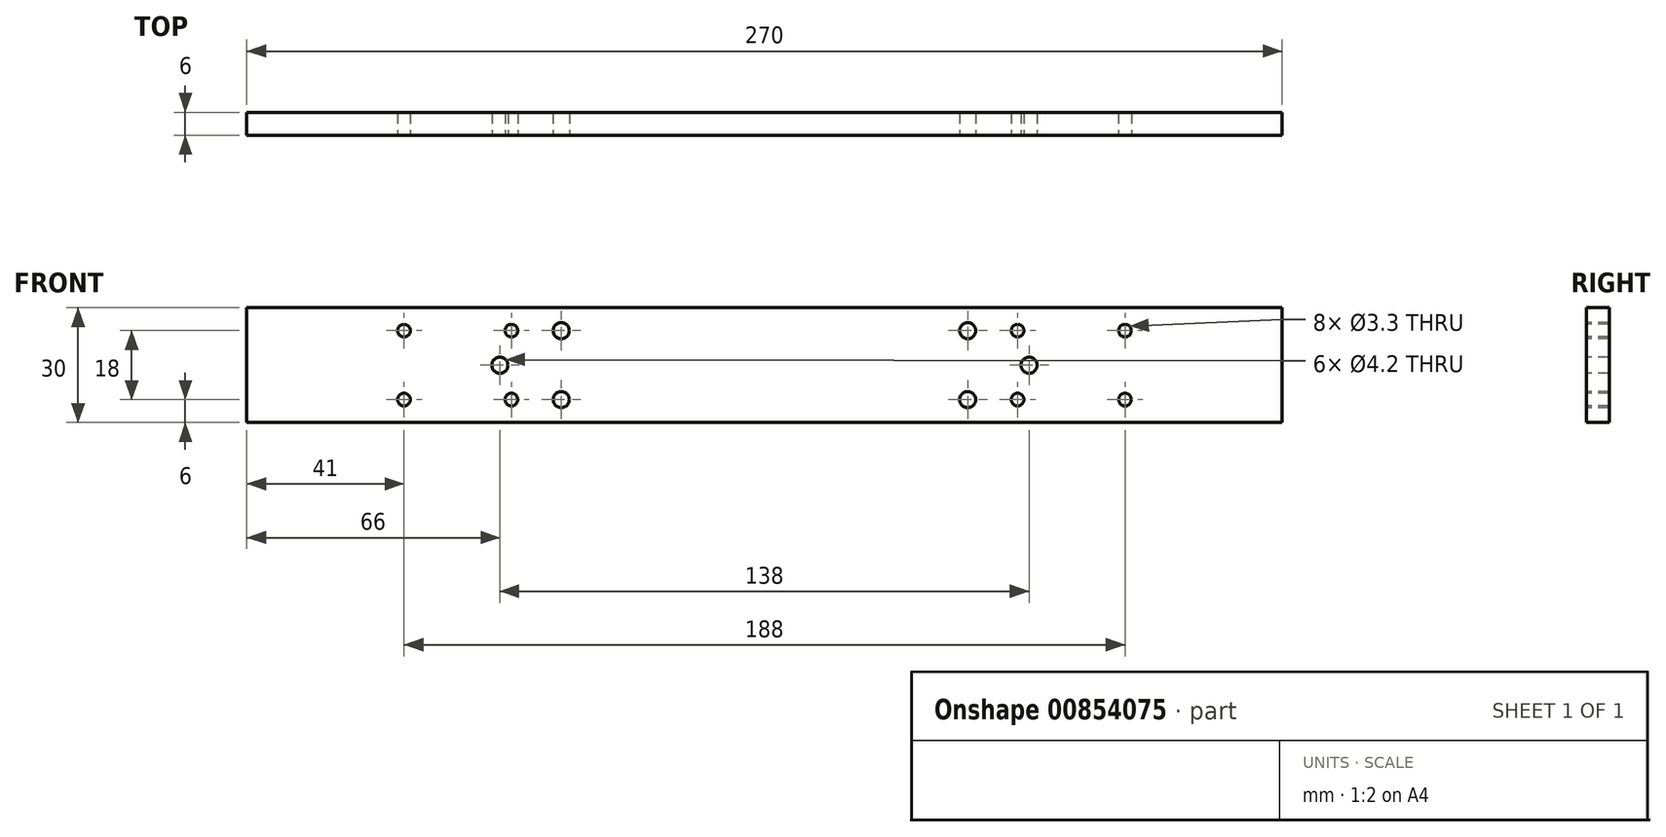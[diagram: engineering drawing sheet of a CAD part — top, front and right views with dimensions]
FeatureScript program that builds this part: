
annotation { "Feature Type Name" : "Feature", "Feature Type Description" : "" }
export const myFeature = defineFeature(function(context is Context, id is Id, definition is map)
    precondition{}
    {
        {
            var Q0;
            Q0=qCreatedBy(makeId("Front.planeOp"),FACE);
            var sketch = newSketch(context, id + "F0", { "sketchPlane" : qUnion([Q0])});
            skLineSegment(sketch, "E0.bottom", {"start": v(0, 0) * mm, "end": v(270, 0) * mm});
            skLineSegment(sketch, "E0.top", {"start": v(0, 30) * mm, "end": v(270, 30) * mm});
            skLineSegment(sketch, "E0.left", {"start": v(0, 0) * mm, "end": v(0, 30) * mm});
            skLineSegment(sketch, "E0.right", {"start": v(270, 0) * mm, "end": v(270, 30) * mm});
            skSolve(sketch);
        }
        {
            var Q0;
            Q0=makeQuery(id+"F0.imprint","IMPRINT",FACE,{"disambiguationData":[TD([[makeQuery(id+"F0.imprint","IMPRINT",EDGE,{"derivedFrom":sQuery(id+"F0.wireOp",EDGE,"E0.bottom")}),1.0]])]});
            extrude(context, id + "F1", {"entities" : qUnion([Q0]), "depth" : 6 * mm, "offsetDistance" : 25 * mm});
        }
        {
            var Q0;
            Q0=qCreatedBy(makeId("Front.planeOp"),FACE);
            var sketch = newSketch(context, id + "F2", { "sketchPlane" : qUnion([Q0])});
            skPoint(sketch, "E1", {"position": v(66, 15) * mm});
            skPoint(sketch, "E2", {"position": v(82, 24) * mm});
            skPoint(sketch, "E3", {"position": v(82, 6) * mm});
            skPoint(sketch, "E4", {"position": v(204, 15) * mm});
            skPoint(sketch, "E5", {"position": v(188, 24) * mm});
            skPoint(sketch, "E6", {"position": v(188, 6) * mm});
            skSolve(sketch);
        }
        {
            var Q0;
            Q0=sQuery(id+"F2.wireOp",VERTEX,"E1");
            var Q1;
            Q1=sQuery(id+"F2.wireOp",VERTEX,"E2");
            var Q2;
            Q2=sQuery(id+"F2.wireOp",VERTEX,"E3");
            var Q3;
            Q3=sQuery(id+"F2.wireOp",VERTEX,"E4");
            var Q4;
            Q4=sQuery(id+"F2.wireOp",VERTEX,"E5");
            var Q5;
            Q5=sQuery(id+"F2.wireOp",VERTEX,"E6");
            var Q6;
            Q6=makeQuery(id+"F1.opExtrude","SWEPT_BODY",BODY,{"disambiguationData":[OSD([sQuery(id+"F0.wireOp",EDGE,"E0.bottom"),sQuery(id+"F0.wireOp",EDGE,"E0.top"),sQuery(id+"F0.wireOp",EDGE,"E0.left"),sQuery(id+"F0.wireOp",EDGE,"E0.right")])]});
            hole(context, id + "F3", {"style" : HoleStyle.SIMPLE, "endStyle" : HoleEndStyle.THROUGH, "oppositeDirection" : true, "standardTappedOrClearance" : lookupTablePath({ "standard" : "ISO", "engagement" : "75%", "pitch" : "0.8 mm", "size" : "M5", "type" : "Tapped" }), "standardBlindInLast" : lookupTablePath({ "standard" : "ISO", "fit" : "Normal", "engagement" : "75%", "pitch" : "0.8 mm", "size" : "M5", "type" : "Clearance & tapped" }), "holeDiameter" : 4.2 * mm, "majorDiameter" : 5 * mm, "showTappedDepth" : true, "isTappedThrough" : true, "tappedDepth" : 12 * mm, "tapClearance" : 3, "locations" : qUnion([Q0, Q1, Q2, Q3, Q4, Q5]), "scope" : qUnion([Q6]), "startStyle" : HoleStartStyle.SKETCH});
        }
        {
            var Q0;
            Q0=qCreatedBy(makeId("Front.planeOp"),FACE);
            var sketch = newSketch(context, id + "F4", { "sketchPlane" : qUnion([Q0])});
            skPoint(sketch, "E7", {"position": v(69, 24) * mm});
            skPoint(sketch, "E8", {"position": v(69, 6) * mm});
            skPoint(sketch, "E9", {"position": v(41, 6) * mm});
            skPoint(sketch, "E10", {"position": v(41, 24) * mm});
            skPoint(sketch, "E11", {"position": v(229, 24) * mm});
            skPoint(sketch, "E12", {"position": v(229, 6) * mm});
            skPoint(sketch, "E13", {"position": v(201, 6) * mm});
            skPoint(sketch, "E14", {"position": v(201, 24) * mm});
            skSolve(sketch);
        }
        {
            var Q0;
            Q0=sQuery(id+"F4.wireOp",VERTEX,"E10");
            var Q1;
            Q1=sQuery(id+"F4.wireOp",VERTEX,"E7");
            var Q2;
            Q2=sQuery(id+"F4.wireOp",VERTEX,"E8");
            var Q3;
            Q3=sQuery(id+"F4.wireOp",VERTEX,"E9");
            var Q4;
            Q4=sQuery(id+"F4.wireOp",VERTEX,"E14");
            var Q5;
            Q5=sQuery(id+"F4.wireOp",VERTEX,"E11");
            var Q6;
            Q6=sQuery(id+"F4.wireOp",VERTEX,"E12");
            var Q7;
            Q7=sQuery(id+"F4.wireOp",VERTEX,"E13");
            var Q8;
            Q8=makeQuery(id+"F1.opExtrude","SWEPT_BODY",BODY,{"disambiguationData":[OSD([sQuery(id+"F0.wireOp",EDGE,"E0.bottom"),sQuery(id+"F0.wireOp",EDGE,"E0.top"),sQuery(id+"F0.wireOp",EDGE,"E0.left"),sQuery(id+"F0.wireOp",EDGE,"E0.right")])]});
            hole(context, id + "F5", {"style" : HoleStyle.SIMPLE, "endStyle" : HoleEndStyle.THROUGH, "oppositeDirection" : true, "standardTappedOrClearance" : lookupTablePath({ "standard" : "ISO", "engagement" : "75%", "pitch" : "0.7 mm", "size" : "M4", "type" : "Tapped" }), "standardBlindInLast" : lookupTablePath({ "standard" : "ISO", "fit" : "Normal", "engagement" : "75%", "pitch" : "0.7 mm", "size" : "M4", "type" : "Clearance & tapped" }), "holeDiameter" : 3.3 * mm, "majorDiameter" : 4 * mm, "showTappedDepth" : true, "isTappedThrough" : true, "tappedDepth" : 12 * mm, "tapClearance" : 3, "locations" : qUnion([Q0, Q1, Q2, Q3, Q4, Q5, Q6, Q7]), "scope" : qUnion([Q8]), "startStyle" : HoleStartStyle.SKETCH});
        }
    });
